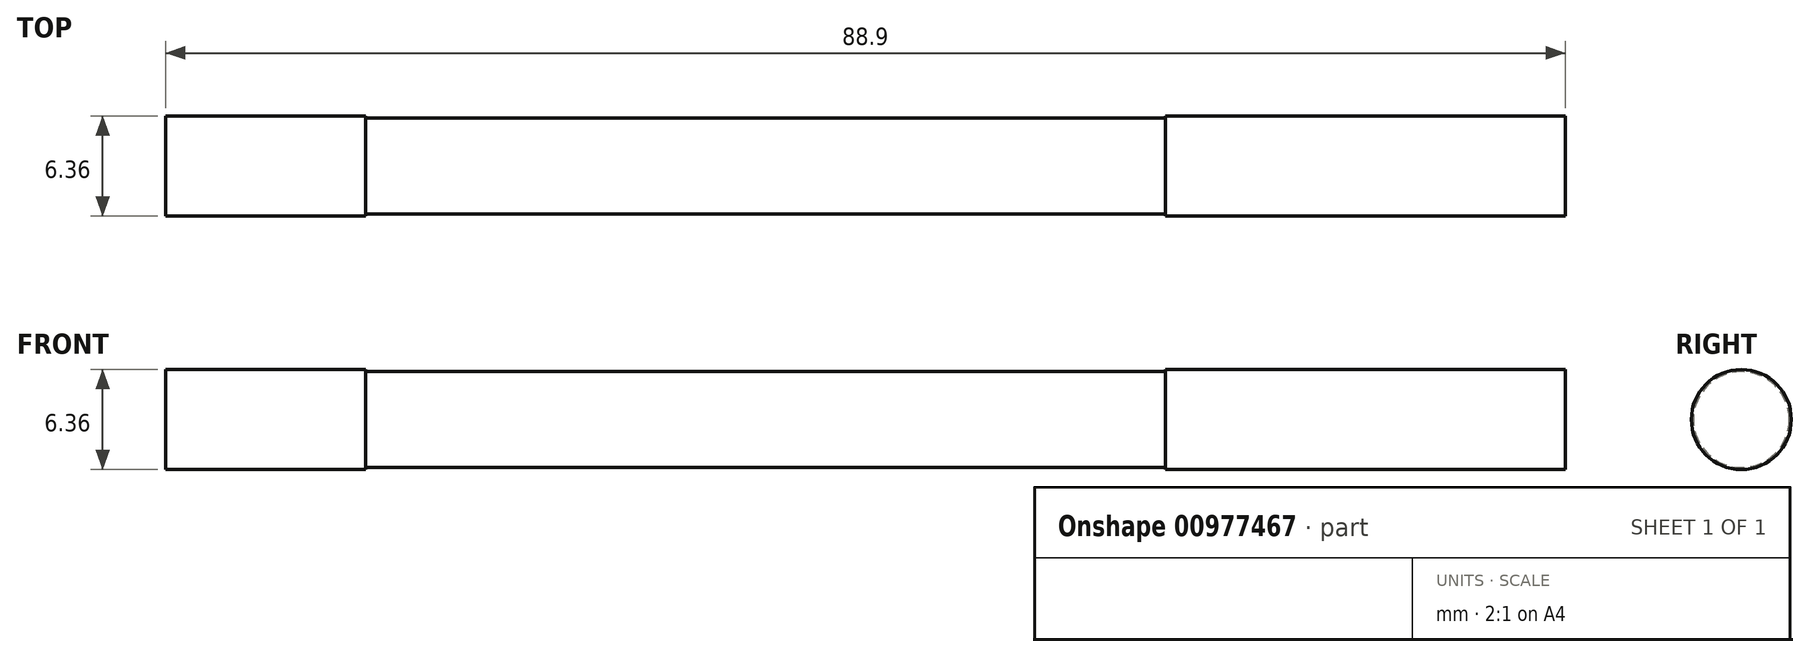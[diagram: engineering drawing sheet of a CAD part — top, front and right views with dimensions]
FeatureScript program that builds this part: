
annotation { "Feature Type Name" : "Feature", "Feature Type Description" : "" }
export const myFeature = defineFeature(function(context is Context, id is Id, definition is map)
    precondition{}
    {
        {
            var Q0;
            Q0=qCreatedBy(makeId("Right.planeOp"),FACE);
            var sketch = newSketch(context, id + "F0", { "sketchPlane" : qUnion([Q0])});
            skCircle(sketch, "E0", {"center": v(0, 0) * mm, "radius": 3.18 * mm});
            skSolve(sketch);
        }
        {
            var Q0;
            Q0 = qSketchRegion(id + "F0", true);
            extrude(context, id + "F1", {"entities" : qUnion([Q0]), "depth" : 12.7 * mm, "offsetDistance" : 25.4 * mm});
        }
        {
            var Q0;
            Q0=makeQuery(id+"F1.opExtrude","CAP_FACE",FACE,{"disambiguationData":[OSD([sQuery(id+"F0.wireOp",EDGE,"E0")])],"isStart":false});
            var sketch = newSketch(context, id + "F2", { "sketchPlane" : qUnion([Q0])});
            skCircle(sketch, "E1", {"center": v(0, 0) * mm, "radius": 3.05 * mm});
            skSolve(sketch);
        }
        {
            var Q0;
            Q0=makeQuery(id+"F2.imprint","IMPRINT",FACE,{"disambiguationData":[TD([[makeQuery(id+"F2.imprint","IMPRINT",EDGE,{"derivedFrom":sQuery(id+"F2.wireOp",EDGE,"E1")}),1.0]])]});
            extrude(context, id + "F3", {"entities" : qUnion([Q0]), "operationType" : NewBodyOperationType.ADD, "depth" : 50.8 * mm, "offsetDistance" : 25.4 * mm});
        }
        {
            var Q0;
            Q0=makeQuery(id+"F3.opExtrude","CAP_FACE",FACE,{"disambiguationData":[OSD([sQuery(id+"F2.wireOp",EDGE,"E1")])],"isStart":false});
            var sketch = newSketch(context, id + "F4", { "sketchPlane" : qUnion([Q0])});
            skCircle(sketch, "E2", {"center": v(0, 0) * mm, "radius": 3.18 * mm});
            skSolve(sketch);
        }
        {
            var Q0;
            Q0 = qSketchRegion(id + "F4", true);
            extrude(context, id + "F5", {"entities" : qUnion([Q0]), "operationType" : NewBodyOperationType.ADD, "depth" : 25.4 * mm, "offsetDistance" : 25.4 * mm});
        }
    });
